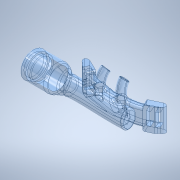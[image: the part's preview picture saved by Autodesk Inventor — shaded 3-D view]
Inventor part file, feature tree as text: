
AUTODESK INVENTOR PART (.ipt)
format: ipt  version: 2020 (Build 240168000, 168)  size: 1,834,496 bytes
history: native  units: in
note: dims shown in document units (in); Inventor stores cm internally (conversion verified against a paired STEP export)
features: fillet x1
ambient origin geometry x8: Origin, YZ Plane, XZ Plane, XY Plane, X Axis, Y Axis, Z Axis, Center Point
bodies: Solid1 (feature_tree)
feature tree (1):
  fillet  "Redondeo44"  [1 undecoded]
note: 1 required parameter value undecoded (feature->parameter linkage not recoverable at this tier; creation-order binding heuristic only, values carry confidence <= 0.55)
